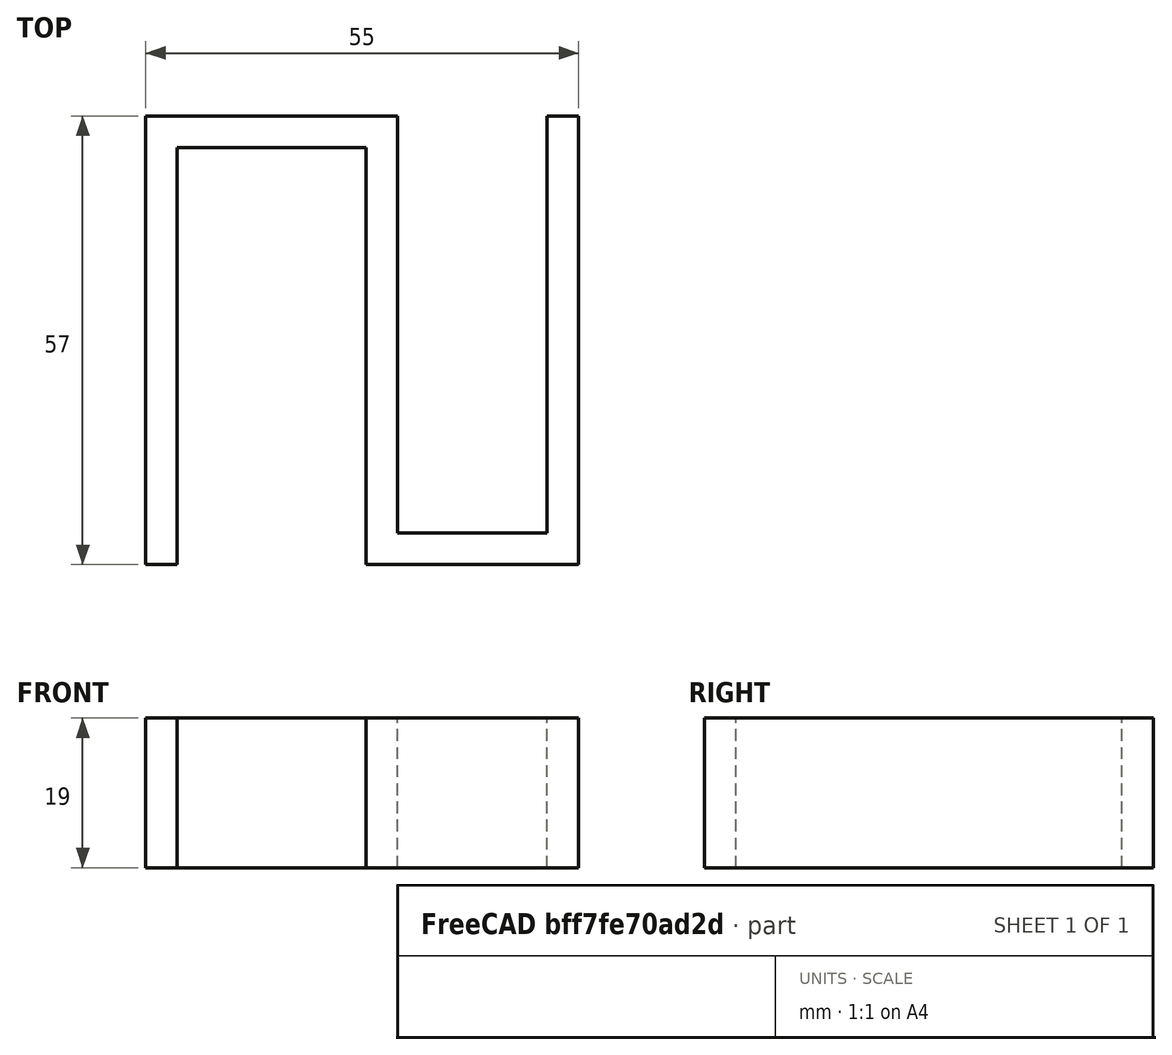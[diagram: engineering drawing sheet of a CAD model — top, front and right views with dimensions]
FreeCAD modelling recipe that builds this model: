
FCSTD DOCUMENT  (FreeCAD 0.20R24612 (Git))
Label: usb_hangers
License: All rights reserved
LicenseURL: http://en.wikipedia.org/wiki/All_rights_reserved
objects: Sketcher::SketchObject×1, PartDesign::Pad×1, PartDesign::Body×1
note: 4 computed .brp shape members not serialized (recipe doc carries the construction recipe); baked Part::Feature solids carry a one-line shape summary decoded from their .brp

FEATURE [Sketcher::SketchObject] Sketch
  FullyConstrained = true
  MapMode = 5
  Support = -> [XY_Plane]
  sketch-geometry (13):
    g0: LineSegment StartX=0 StartY=0 StartZ=0 EndX=0 EndY=53 EndZ=0
    g1: LineSegment StartX=0 StartY=53 StartZ=0 EndX=24 EndY=53 EndZ=0
    g2: LineSegment StartX=24 StartY=53 StartZ=0 EndX=24 EndY=6.55831e-11 EndZ=0
    g3: LineSegment StartX=24 StartY=6.55862e-11 StartZ=0 EndX=51 EndY=-9.21669e-11 EndZ=0
    g4: LineSegment StartX=51 StartY=-9.21669e-11 StartZ=0 EndX=51 EndY=57 EndZ=0
    g5: LineSegment StartX=51 StartY=57 StartZ=0 EndX=47 EndY=57 EndZ=0
    g6: LineSegment StartX=47 StartY=57 StartZ=0 EndX=47 EndY=4 EndZ=0
    g7: LineSegment StartX=28 StartY=4 StartZ=0 EndX=28 EndY=57 EndZ=0
    g8: LineSegment StartX=28 StartY=57 StartZ=0 EndX=-4 EndY=57 EndZ=0
    g9: LineSegment StartX=-4 StartY=57 StartZ=0 EndX=-4 EndY=0 EndZ=0
    g10: LineSegment StartX=-4 StartY=0 StartZ=0 EndX=0 EndY=0 EndZ=0
    g11: LineSegment StartX=28 StartY=4 StartZ=0 EndX=47 EndY=4 EndZ=0
    g12: LineSegment StartX=28 StartY=57 StartZ=0 EndX=47 EndY=57 EndZ=0
  constraints (37):
    c: Coincident(g-1,g0)
    c: Vertical(g0)
    c: Coincident(g0,g1)
    c: Horizontal(g1)
    c: Coincident(g1,g2)
    c: Coincident(g2,g3)
    c: Coincident(g3,g4)
    c: Coincident(g4,g5)
    c: Coincident(g5,g6)
    c: Coincident(g7,g8)
    c: Horizontal(g8)
    c: Coincident(g8,g9)
    c: PointOnObject(g9,g-1)
    c: Vertical(g9)
    c: Coincident(g9,g10)
    c: Coincident(g10,g0)
    c: Distance(g0) = 53
    c: Distance(g1) = 24
    c: Parallel(g2,g7)
    c: Parallel(g6,g4)
    c: Horizontal(g5)
    c: DistanceX(g0,g2) = 24
    c: DistanceX(g8,g0) = 4
    c: DistanceY(g0,g8) = 4
    c: Coincident(g11,g6)
    c: Distance(g11) = 19
    c: Parallel(g11,g3)
    c: Coincident(g12,g7)
    c: Coincident(g12,g5)
    c: Horizontal(g12)
    c: Coincident(g11,g7)
    c: Parallel(g6,g7)
    c: Distance(g7,g2) = 4
    c: Distance(g6,g4) = 4
    c: Distance(g6,g3) = 4
    c: Angle(g11,g7) = 1.5708
    c: DistanceY(g7,g7) = 53
FEATURE [PartDesign::Pad] Pad
  AllowMultiFace = false
  Direction = (0,0,1)
  Length = 19
  Length2 = 100
  Profile = -> Sketch
  Type = 0
FEATURE [PartDesign::Body] Body
  Group = -> [Sketch,Pad]
  Origin = -> Origin
  Tip = -> Pad
